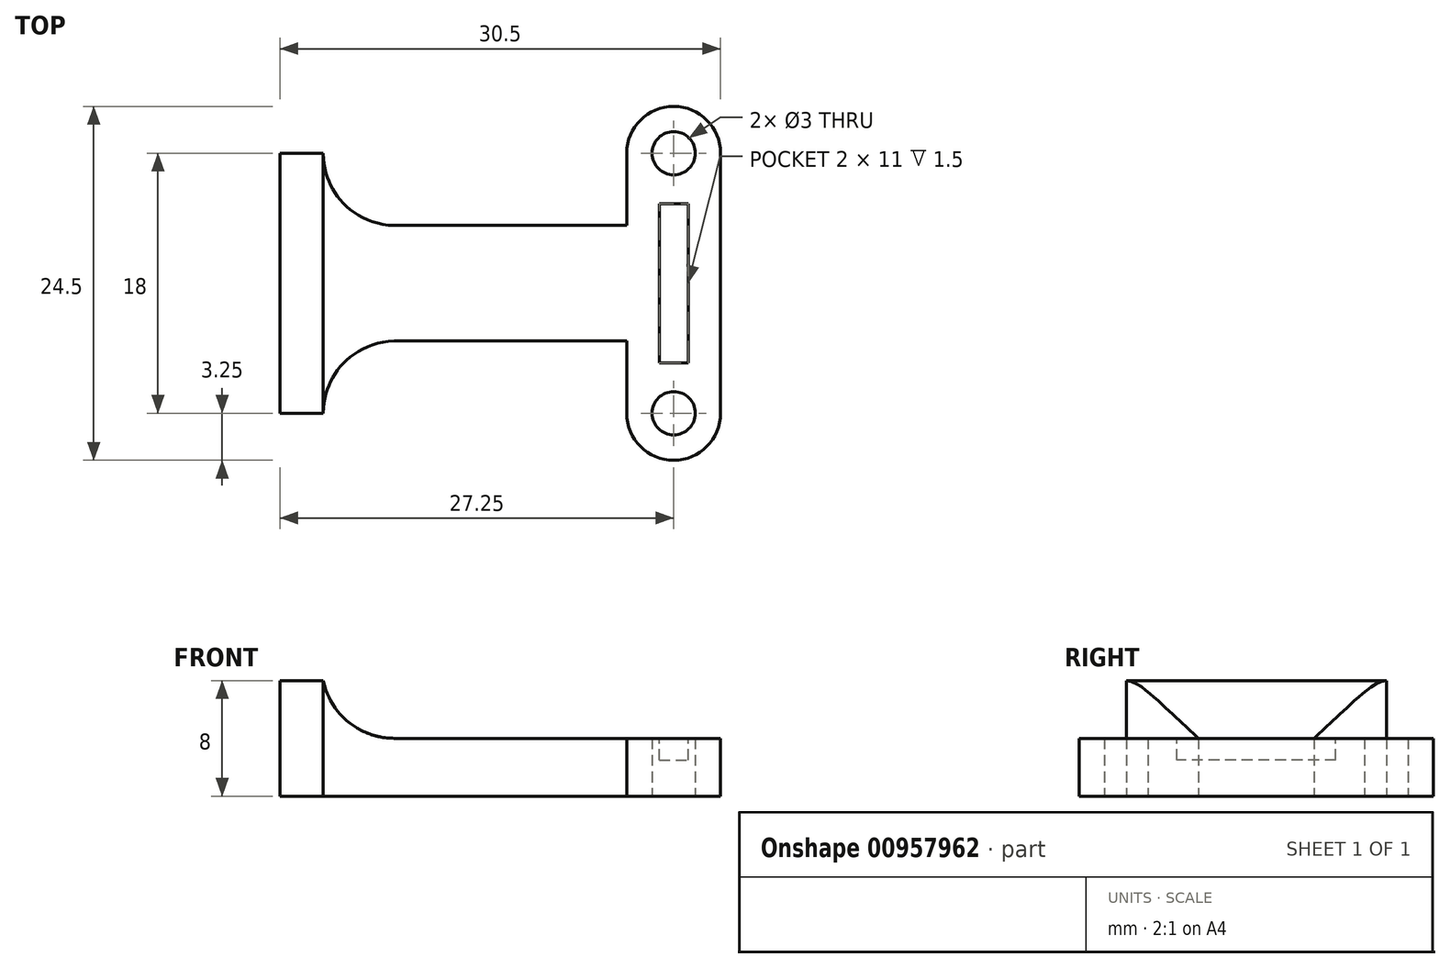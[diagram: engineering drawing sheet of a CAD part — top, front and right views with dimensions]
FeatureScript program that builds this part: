
annotation { "Feature Type Name" : "Feature", "Feature Type Description" : "" }
export const myFeature = defineFeature(function(context is Context, id is Id, definition is map)
    precondition{}
    {
        {
            var Q0;
            Q0=qCreatedBy(makeId("Top.planeOp"),FACE);
            var sketch = newSketch(context, id + "F0", { "sketchPlane" : qUnion([Q0])});
            skPoint(sketch, "E0.middle", {"position": v(0, 0) * mm});
            skCircle(sketch, "E1", {"center": v(0, 9) * mm, "radius": 1.5 * mm});
            skCircle(sketch, "E2", {"center": v(0, -9) * mm, "radius": 1.5 * mm});
            skLineSegment(sketch, "E3", {"start": v(0, -9) * mm, "end": v(0, 9) * mm, "construction": true});
            skCircle(sketch, "E4", {"center": v(0, 9) * mm, "radius": 3.25 * mm});
            skCircle(sketch, "E5", {"center": v(0, -9) * mm, "radius": 3.25 * mm});
            skLineSegment(sketch, "E6", {"start": v(3.25, -9) * mm, "end": v(3.25, 9) * mm});
            skLineSegment(sketch, "E7", {"start": v(-3.25, -9) * mm, "end": v(-3.25, 9) * mm});
            skLineSegment(sketch, "E8.bottom", {"start": v(-3.25, 4) * mm, "end": v(-27.25, 4) * mm});
            skLineSegment(sketch, "E8.top", {"start": v(-3.25, -4) * mm, "end": v(-27.25, -4) * mm});
            skLineSegment(sketch, "E8.left", {"start": v(-3.25, 4) * mm, "end": v(-3.25, -4) * mm});
            skLineSegment(sketch, "E8.right", {"start": v(-27.25, 4) * mm, "end": v(-27.25, -4) * mm});
            skPoint(sketch, "E9", {"position": v(-3.25, 0) * mm});
            skLineSegment(sketch, "E10.bottom", {"start": v(-27.25, 9) * mm, "end": v(-24.25, 9) * mm});
            skLineSegment(sketch, "E10.top", {"start": v(-27.25, -9) * mm, "end": v(-24.25, -9) * mm});
            skLineSegment(sketch, "E10.left", {"start": v(-27.25, 9) * mm, "end": v(-27.25, -9) * mm});
            skLineSegment(sketch, "E10.right", {"start": v(-24.25, 9) * mm, "end": v(-24.25, -9) * mm});
            skPoint(sketch, "E11", {"position": v(-24.25, 0) * mm});
            skSolve(sketch);
        }
        {
            var Q0;
            Q0 = qSketchRegion(id + "F0", true);
            extrude(context, id + "F1", {"entities" : qUnion([Q0]), "depth" : 4 * mm, "offsetDistance" : 25 * mm});
        }
        {
            var Q0;
            Q0=makeQuery(id+"F1.opExtrude","CAP_FACE",FACE,{"disambiguationData":[OSD([sQuery(id+"F0.wireOp",EDGE,"E1"),sQuery(id+"F0.wireOp",EDGE,"E2"),sQuery(id+"F0.wireOp",EDGE,"E4"),sQuery(id+"F0.wireOp",EDGE,"E5"),sQuery(id+"F0.wireOp",EDGE,"E6"),sQuery(id+"F0.wireOp",EDGE,"E7"),sQuery(id+"F0.wireOp",EDGE,"E8.bottom"),sQuery(id+"F0.wireOp",EDGE,"E8.top"),sQuery(id+"F0.wireOp",EDGE,"E8.right")])],"isStart":false});
            var sketch = newSketch(context, id + "F2", { "sketchPlane" : qUnion([Q0])});
            skLineSegment(sketch, "E12.bottom", {"start": v(-1, 5.5) * mm, "end": v(1, 5.5) * mm});
            skLineSegment(sketch, "E12.top", {"start": v(-1, -5.5) * mm, "end": v(1, -5.5) * mm});
            skLineSegment(sketch, "E12.left", {"start": v(-1, 5.5) * mm, "end": v(-1, -5.5) * mm});
            skLineSegment(sketch, "E12.right", {"start": v(1, 5.5) * mm, "end": v(1, -5.5) * mm});
            skPoint(sketch, "E13", {"position": v(0, 5.5) * mm});
            skSolve(sketch);
        }
        {
            var Q0;
            Q0=makeQuery(id+"F2.imprint","IMPRINT",FACE,{"disambiguationData":[TD([[makeQuery(id+"F2.imprint","IMPRINT",EDGE,{"derivedFrom":sQuery(id+"F2.wireOp",EDGE,"E12.bottom")}),-1.0]])]});
            extrude(context, id + "F3", {"entities" : qUnion([Q0]), "operationType" : NewBodyOperationType.REMOVE, "oppositeDirection" : true, "depth" : 1.5 * mm, "offsetDistance" : 25 * mm});
        }
        {
            var Q0;
            {var subQ5=sQuery(id+"F0.wireOp",EDGE,"E10.bottom");Q0=makeQuery(id+"F0.imprint","IMPRINT",FACE,{"disambiguationData":[TD([[makeQuery(id+"F0.imprint","IMPRINT",EDGE,{"derivedFrom":subQ5}),-1.0]])]});}
            var Q1;
            {var subQ0=sQuery(id+"F0.wireOp",EDGE,"E10.left");var subQ1=sQuery(id+"F0.wireOp",EDGE,"E8.bottom");var subQ2=makeQuery(id+"F0.imprint","INTERSECT",VERTEX,{"derivedFrom":[subQ1,subQ0]});Q1=makeQuery(id+"F0.imprint","IMPRINT",FACE,{"disambiguationData":[TD([[makeQuery(id+"F0.imprint","IMPRINT",EDGE,{"disambiguationData":[TD([[subQ2,1.0]])],"derivedFrom":subQ1}),1.0]])]});}
            var Q2;
            {var subQ5=sQuery(id+"F0.wireOp",EDGE,"E10.top");Q2=makeQuery(id+"F0.imprint","IMPRINT",FACE,{"disambiguationData":[TD([[makeQuery(id+"F0.imprint","IMPRINT",EDGE,{"derivedFrom":subQ5}),1.0]])]});}
            extrude(context, id + "F4", {"entities" : qUnion([Q0, Q1, Q2]), "operationType" : NewBodyOperationType.ADD, "depth" : 8 * mm, "offsetDistance" : 25 * mm});
        }
        {
            var Q0;
            Q0=makeQuery(id+"F1.opExtrude","SWEPT_EDGE",EDGE,{"disambiguationData":[OSD([sQuery(id+"F0.wireOp",EDGE,"E8.bottom"),sQuery(id+"F0.wireOp",EDGE,"E10.right")])]});
            var Q1;
            Q1=makeQuery(id+"F1.opExtrude","SWEPT_EDGE",EDGE,{"disambiguationData":[OSD([sQuery(id+"F0.wireOp",EDGE,"E8.top"),sQuery(id+"F0.wireOp",EDGE,"E10.right")])]});
            var Q2;
            {var subQ0=sQuery(id+"F0.wireOp",EDGE,"E10.right");Q2=makeQuery(id+"F4.boolean.opBoolean","INTERSECT",EDGE,{"derivedFrom":[makeQuery(id+"F1.opExtrude","CAP_FACE",FACE,{"disambiguationData":[OSD([sQuery(id+"F0.wireOp",EDGE,"E1"),sQuery(id+"F0.wireOp",EDGE,"E2"),sQuery(id+"F0.wireOp",EDGE,"E4"),sQuery(id+"F0.wireOp",EDGE,"E5"),sQuery(id+"F0.wireOp",EDGE,"E6"),sQuery(id+"F0.wireOp",EDGE,"E7"),sQuery(id+"F0.wireOp",EDGE,"E8.bottom"),sQuery(id+"F0.wireOp",EDGE,"E8.top"),sQuery(id+"F0.wireOp",EDGE,"E10.bottom"),sQuery(id+"F0.wireOp",EDGE,"E10.top"),sQuery(id+"F0.wireOp",EDGE,"E10.left"),subQ0])],"isStart":false}),makeQuery(id+"F4.opExtrude","SWEPT_FACE",FACE,{"disambiguationData":[OSD([subQ0])]})]});}
            fillet(context, id + "F5", {"entities" : qUnion([Q0, Q1, Q2]), "radius" : 5 * mm, "tangentPropagation" : true, "allowEdgeOverflow" : false});
        }
    });
